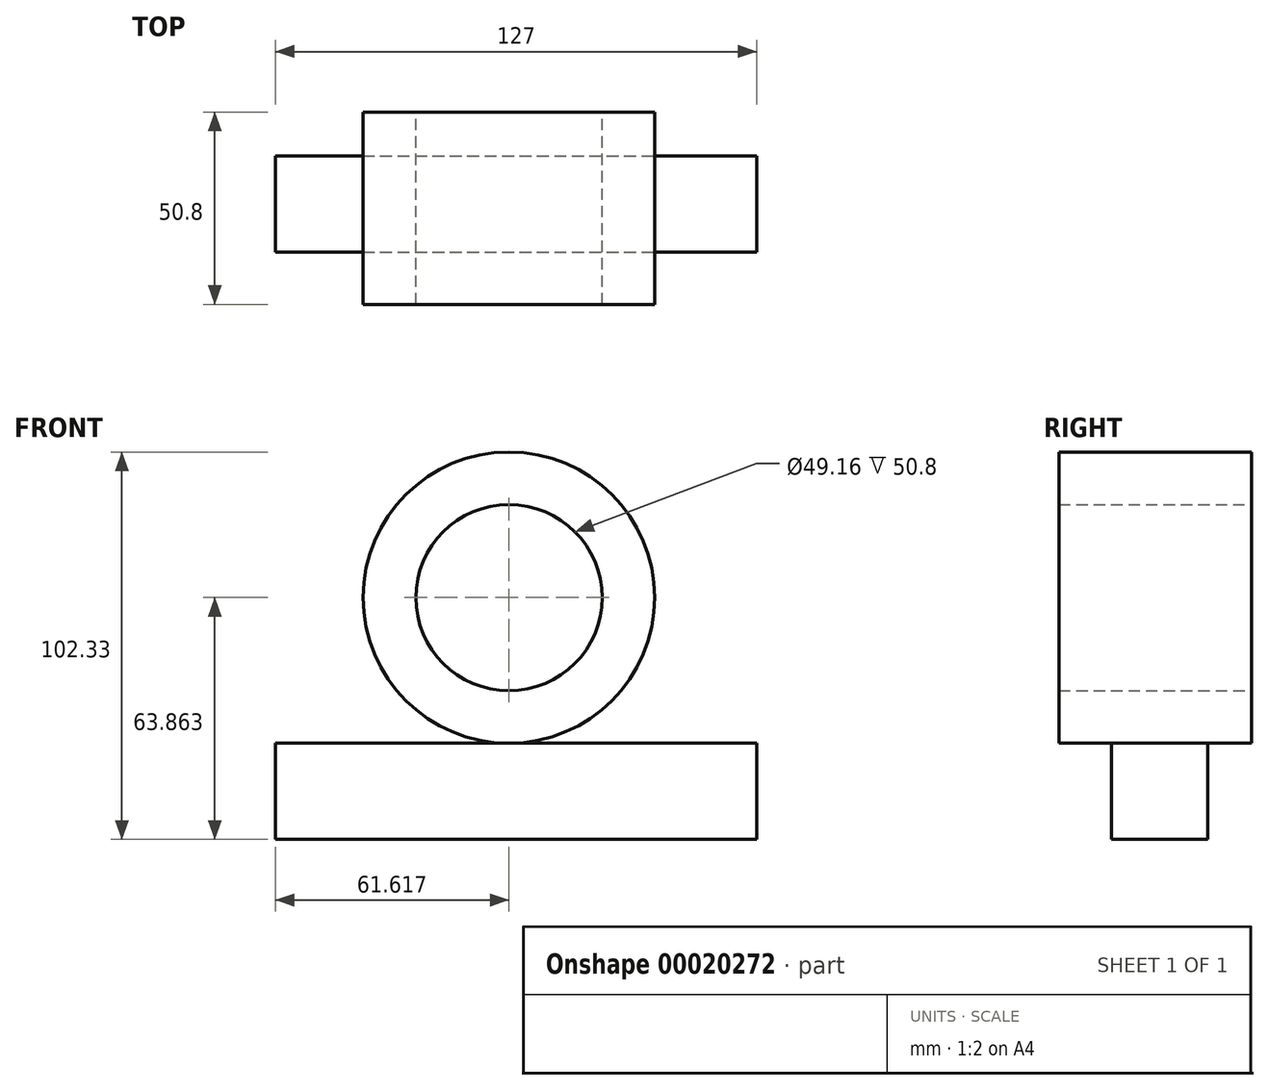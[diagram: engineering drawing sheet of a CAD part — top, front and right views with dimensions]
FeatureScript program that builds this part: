
annotation { "Feature Type Name" : "Feature", "Feature Type Description" : "" }
export const myFeature = defineFeature(function(context is Context, id is Id, definition is map)
    precondition{}
    {
        {
            var Q0;
            Q0=qCreatedBy(makeId("Top.planeOp"),FACE);
            var sketch = newSketch(context, id + "F0", { "sketchPlane" : qUnion([Q0])});
            skLineSegment(sketch, "E0.bottom", {"start": v(-45.62, 13.83) * mm, "end": v(81.38, 13.83) * mm});
            skLineSegment(sketch, "E0.top", {"start": v(-45.62, -11.57) * mm, "end": v(81.38, -11.57) * mm});
            skLineSegment(sketch, "E0.left", {"start": v(-45.62, 13.83) * mm, "end": v(-45.62, -11.57) * mm});
            skLineSegment(sketch, "E0.right", {"start": v(81.38, 13.83) * mm, "end": v(81.38, -11.57) * mm});
            skSolve(sketch);
        }
        {
            var Q0;
            Q0 = qSketchRegion(id + "F0", true);
            extrude(context, id + "F1", {"entities" : qUnion([Q0]), "depth" : 25.4 * mm});
        }
        {
            var Q0;
            Q0=qCreatedBy(makeId("Front.planeOp"),FACE);
            var sketch = newSketch(context, id + "F2", { "sketchPlane" : qUnion([Q0])});
            skCircle(sketch, "E1", {"center": v(16, 63.86) * mm, "radius": 38.46 * mm});
            skCircle(sketch, "E2", {"center": v(16, 63.86) * mm, "radius": 24.58 * mm});
            skSolve(sketch);
        }
        {
            var Q0;
            Q0 = qSketchRegion(id + "F2", true);
            extrude(context, id + "F3", {"entities" : qUnion([Q0]), "operationType" : NewBodyOperationType.ADD, "depth" : 25.4 * mm, "hasSecondDirection" : true, "secondDirectionOppositeDirection" : true, "secondDirectionDepth" : 25.4 * mm});
        }
    });
